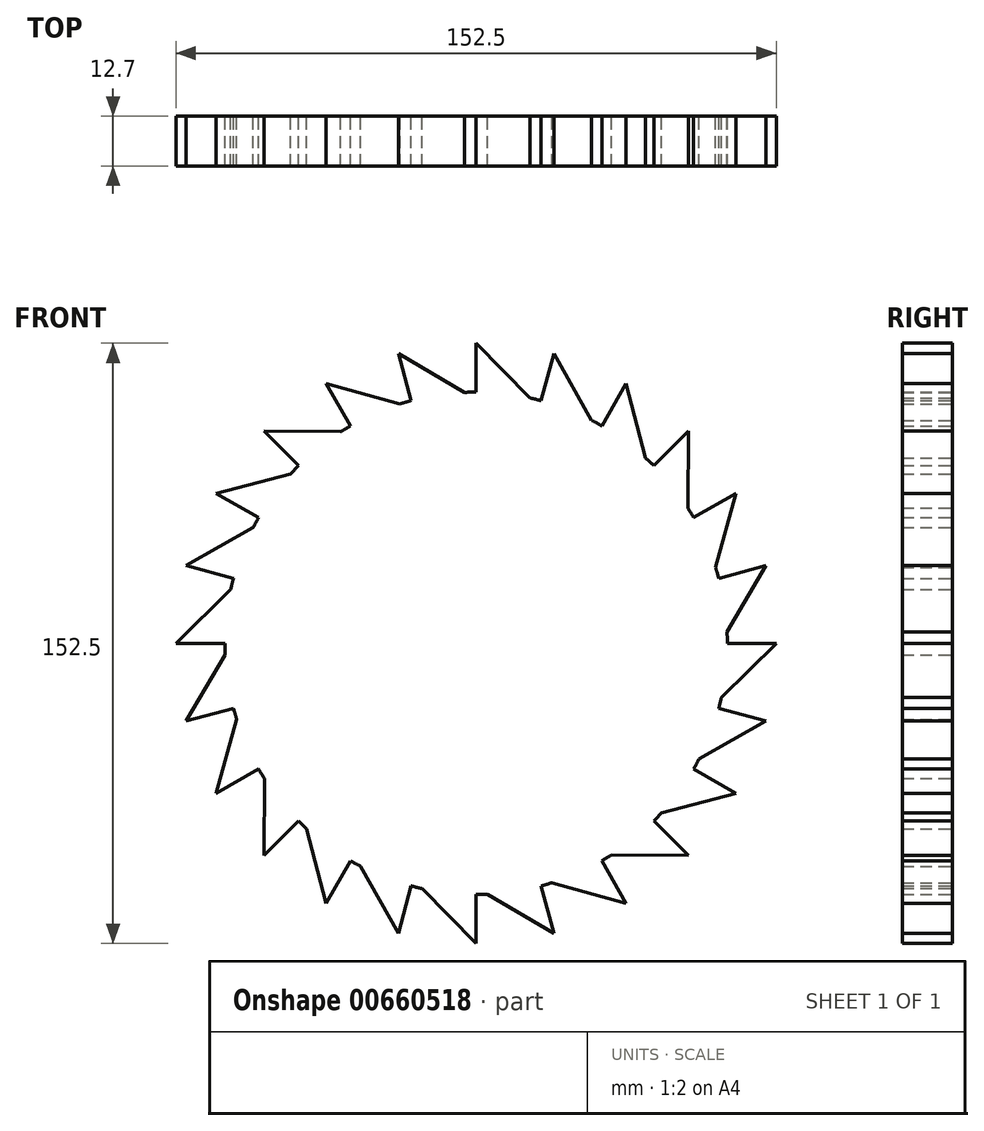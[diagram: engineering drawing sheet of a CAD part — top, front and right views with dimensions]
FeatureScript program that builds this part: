
annotation { "Feature Type Name" : "Feature", "Feature Type Description" : "" }
export const myFeature = defineFeature(function(context is Context, id is Id, definition is map)
    precondition{}
    {
        {
            var Q0;
            Q0=qCreatedBy(makeId("Front.planeOp"),FACE);
            var sketch = newSketch(context, id + "F0", { "sketchPlane" : qUnion([Q0])});
            skCircle(sketch, "E0", {"center": v(0, 0) * mm, "radius": 63.5 * mm, "construction": true});
            skLineSegment(sketch, "E1", {"start": v(0, 63.5) * mm, "end": v(0, 76.25) * mm});
            skLineSegment(sketch, "E2", {"start": v(0, 76.25) * mm, "end": v(14.11, 61.91) * mm});
            skLineSegment(sketch, "E3.1.1", {"start": v(-16.44, 61.34) * mm, "end": v(-19.73, 73.65) * mm});
            skLineSegment(sketch, "E3.1.2", {"start": v(-19.73, 73.65) * mm, "end": v(-2.4, 63.45) * mm});
            skLineSegment(sketch, "E3.2.1", {"start": v(-31.75, 55) * mm, "end": v(-38.13, 66.03) * mm});
            skLineSegment(sketch, "E3.2.2", {"start": v(-38.13, 66.03) * mm, "end": v(-18.74, 60.67) * mm});
            skLineSegment(sketch, "E4.2.3.0", {"start": v(-44.9, 44.9) * mm, "end": v(-53.92, 53.92) * mm});
            skLineSegment(sketch, "E4.5.3.0", {"start": v(-53.92, 53.92) * mm, "end": v(-33.8, 53.76) * mm});
            skLineSegment(sketch, "E4.2.4.0", {"start": v(-55, 31.75) * mm, "end": v(-66.03, 38.13) * mm});
            skLineSegment(sketch, "E4.5.4.0", {"start": v(-66.03, 38.13) * mm, "end": v(-46.56, 43.18) * mm});
            skLineSegment(sketch, "E4.2.5.0", {"start": v(-61.34, 16.44) * mm, "end": v(-73.65, 19.73) * mm});
            skLineSegment(sketch, "E4.5.5.0", {"start": v(-73.65, 19.73) * mm, "end": v(-56.15, 29.65) * mm});
            skLineSegment(sketch, "E4.2.6.0", {"start": v(-63.5, 0) * mm, "end": v(-76.25, 0) * mm});
            skLineSegment(sketch, "E4.5.6.0", {"start": v(-76.25, 0) * mm, "end": v(-61.91, 14.11) * mm});
            skLineSegment(sketch, "E4.2.7.0", {"start": v(-61.34, -16.44) * mm, "end": v(-73.65, -19.73) * mm});
            skLineSegment(sketch, "E4.5.7.0", {"start": v(-73.65, -19.73) * mm, "end": v(-63.45, -2.4) * mm});
            skLineSegment(sketch, "E4.2.8.0", {"start": v(-55, -31.75) * mm, "end": v(-66.03, -38.13) * mm});
            skLineSegment(sketch, "E4.5.8.0", {"start": v(-66.03, -38.13) * mm, "end": v(-60.67, -18.74) * mm});
            skLineSegment(sketch, "E4.2.9.0", {"start": v(-44.9, -44.9) * mm, "end": v(-53.92, -53.92) * mm});
            skLineSegment(sketch, "E4.5.9.0", {"start": v(-53.92, -53.92) * mm, "end": v(-53.76, -33.8) * mm});
            skLineSegment(sketch, "E4.2.10.0", {"start": v(-31.75, -55) * mm, "end": v(-38.13, -66.03) * mm});
            skLineSegment(sketch, "E4.5.10.0", {"start": v(-38.13, -66.03) * mm, "end": v(-43.18, -46.56) * mm});
            skLineSegment(sketch, "E4.2.11.0", {"start": v(-16.44, -61.34) * mm, "end": v(-19.73, -73.65) * mm});
            skLineSegment(sketch, "E4.5.11.0", {"start": v(-19.73, -73.65) * mm, "end": v(-29.65, -56.15) * mm});
            skLineSegment(sketch, "E4.2.12.0", {"start": v(0, -63.5) * mm, "end": v(0, -76.25) * mm});
            skLineSegment(sketch, "E4.5.12.0", {"start": v(0, -76.25) * mm, "end": v(-14.11, -61.91) * mm});
            skLineSegment(sketch, "E4.2.13.0", {"start": v(16.44, -61.34) * mm, "end": v(19.73, -73.65) * mm});
            skLineSegment(sketch, "E4.5.13.0", {"start": v(19.73, -73.65) * mm, "end": v(2.4, -63.45) * mm});
            skLineSegment(sketch, "E4.2.14.0", {"start": v(31.75, -55) * mm, "end": v(38.13, -66.03) * mm});
            skLineSegment(sketch, "E4.5.14.0", {"start": v(38.13, -66.03) * mm, "end": v(18.74, -60.67) * mm});
            skLineSegment(sketch, "E4.2.15.0", {"start": v(44.9, -44.9) * mm, "end": v(53.92, -53.92) * mm});
            skLineSegment(sketch, "E4.5.15.0", {"start": v(53.92, -53.92) * mm, "end": v(33.8, -53.76) * mm});
            skLineSegment(sketch, "E4.2.16.0", {"start": v(55, -31.75) * mm, "end": v(66.03, -38.13) * mm});
            skLineSegment(sketch, "E4.5.16.0", {"start": v(66.03, -38.13) * mm, "end": v(46.56, -43.18) * mm});
            skLineSegment(sketch, "E4.2.17.0", {"start": v(61.34, -16.44) * mm, "end": v(73.65, -19.73) * mm});
            skLineSegment(sketch, "E4.5.17.0", {"start": v(73.65, -19.73) * mm, "end": v(56.15, -29.65) * mm});
            skLineSegment(sketch, "E4.2.18.0", {"start": v(63.5, 0) * mm, "end": v(76.25, 0) * mm});
            skLineSegment(sketch, "E4.5.18.0", {"start": v(76.25, 0) * mm, "end": v(61.91, -14.11) * mm});
            skLineSegment(sketch, "E4.2.19.0", {"start": v(61.34, 16.44) * mm, "end": v(73.65, 19.73) * mm});
            skLineSegment(sketch, "E4.5.19.0", {"start": v(73.65, 19.73) * mm, "end": v(63.45, 2.4) * mm});
            skLineSegment(sketch, "E4.2.20.0", {"start": v(55, 31.75) * mm, "end": v(66.03, 38.13) * mm});
            skLineSegment(sketch, "E4.5.20.0", {"start": v(66.03, 38.13) * mm, "end": v(60.67, 18.74) * mm});
            skLineSegment(sketch, "E4.2.21.0", {"start": v(44.9, 44.9) * mm, "end": v(53.92, 53.92) * mm});
            skLineSegment(sketch, "E4.5.21.0", {"start": v(53.92, 53.92) * mm, "end": v(53.76, 33.8) * mm});
            skLineSegment(sketch, "E4.2.22.0", {"start": v(31.75, 55) * mm, "end": v(38.13, 66.03) * mm});
            skLineSegment(sketch, "E4.5.22.0", {"start": v(38.13, 66.03) * mm, "end": v(43.18, 46.56) * mm});
            skLineSegment(sketch, "E4.2.23.0", {"start": v(16.44, 61.34) * mm, "end": v(19.73, 73.65) * mm});
            skLineSegment(sketch, "E4.5.23.0", {"start": v(19.73, 73.65) * mm, "end": v(29.65, 56.15) * mm});
            skCircle(sketch, "E5", {"center": v(0, 0) * mm, "radius": 63.82 * mm});
            skSolve(sketch);
        }
        {
            var Q0;
            {var subQ0=sQuery(id+"F0.wireOp",EDGE,"E5");var subQ33=makeQuery(id+"F0.imprint","INTERSECT",VERTEX,{"derivedFrom":[sQuery(id+"F0.wireOp",EDGE,"E4.2.18.0"),subQ0]});Q0=makeQuery(id+"F0.imprint","IMPRINT",FACE,{"disambiguationData":[TD([[makeQuery(id+"F0.imprint","IMPRINT",EDGE,{"disambiguationData":[TD([[subQ33,-1.0]])],"derivedFrom":subQ0}),1.0]])]});}
            var Q1;
            {var subQ0=sQuery(id+"F0.wireOp",EDGE,"E4.5.3.0");var subQ1=sQuery(id+"F0.wireOp",EDGE,"E4.2.3.0");var subQ2=makeQuery(id+"F0.imprint","INTERSECT",VERTEX,{"derivedFrom":[subQ1,subQ0]});Q1=makeQuery(id+"F0.imprint","IMPRINT",FACE,{"disambiguationData":[TD([[makeQuery(id+"F0.imprint","IMPRINT",EDGE,{"disambiguationData":[TD([[subQ2,1.0]])],"derivedFrom":subQ1}),-1.0]])]});}
            var Q2;
            {var subQ0=sQuery(id+"F0.wireOp",EDGE,"E3.2.2");var subQ1=sQuery(id+"F0.wireOp",EDGE,"E3.2.1");var subQ2=makeQuery(id+"F0.imprint","INTERSECT",VERTEX,{"derivedFrom":[subQ1,subQ0]});Q2=makeQuery(id+"F0.imprint","IMPRINT",FACE,{"disambiguationData":[TD([[makeQuery(id+"F0.imprint","IMPRINT",EDGE,{"disambiguationData":[TD([[subQ2,1.0]])],"derivedFrom":subQ1}),-1.0]])]});}
            var Q3;
            {var subQ0=sQuery(id+"F0.wireOp",EDGE,"E3.1.2");var subQ1=sQuery(id+"F0.wireOp",EDGE,"E3.1.1");var subQ2=makeQuery(id+"F0.imprint","INTERSECT",VERTEX,{"derivedFrom":[subQ1,subQ0]});Q3=makeQuery(id+"F0.imprint","IMPRINT",FACE,{"disambiguationData":[TD([[makeQuery(id+"F0.imprint","IMPRINT",EDGE,{"disambiguationData":[TD([[subQ2,1.0]])],"derivedFrom":subQ1}),-1.0]])]});}
            var Q4;
            {var subQ0=sQuery(id+"F0.wireOp",EDGE,"E2");var subQ1=sQuery(id+"F0.wireOp",EDGE,"E1");var subQ2=makeQuery(id+"F0.imprint","INTERSECT",VERTEX,{"derivedFrom":[subQ1,subQ0]});Q4=makeQuery(id+"F0.imprint","IMPRINT",FACE,{"disambiguationData":[TD([[makeQuery(id+"F0.imprint","IMPRINT",EDGE,{"disambiguationData":[TD([[subQ2,1.0]])],"derivedFrom":subQ1}),-1.0]])]});}
            var Q5;
            {var subQ0=sQuery(id+"F0.wireOp",EDGE,"E4.5.23.0");var subQ1=sQuery(id+"F0.wireOp",EDGE,"E4.2.23.0");var subQ2=makeQuery(id+"F0.imprint","INTERSECT",VERTEX,{"derivedFrom":[subQ1,subQ0]});Q5=makeQuery(id+"F0.imprint","IMPRINT",FACE,{"disambiguationData":[TD([[makeQuery(id+"F0.imprint","IMPRINT",EDGE,{"disambiguationData":[TD([[subQ2,1.0]])],"derivedFrom":subQ1}),-1.0]])]});}
            var Q6;
            {var subQ0=sQuery(id+"F0.wireOp",EDGE,"E4.5.22.0");var subQ1=sQuery(id+"F0.wireOp",EDGE,"E4.2.22.0");var subQ2=makeQuery(id+"F0.imprint","INTERSECT",VERTEX,{"derivedFrom":[subQ1,subQ0]});Q6=makeQuery(id+"F0.imprint","IMPRINT",FACE,{"disambiguationData":[TD([[makeQuery(id+"F0.imprint","IMPRINT",EDGE,{"disambiguationData":[TD([[subQ2,1.0]])],"derivedFrom":subQ1}),-1.0]])]});}
            var Q7;
            {var subQ0=sQuery(id+"F0.wireOp",EDGE,"E4.5.21.0");var subQ1=sQuery(id+"F0.wireOp",EDGE,"E4.2.21.0");var subQ2=makeQuery(id+"F0.imprint","INTERSECT",VERTEX,{"derivedFrom":[subQ1,subQ0]});Q7=makeQuery(id+"F0.imprint","IMPRINT",FACE,{"disambiguationData":[TD([[makeQuery(id+"F0.imprint","IMPRINT",EDGE,{"disambiguationData":[TD([[subQ2,1.0]])],"derivedFrom":subQ1}),-1.0]])]});}
            var Q8;
            {var subQ0=sQuery(id+"F0.wireOp",EDGE,"E4.5.20.0");var subQ1=sQuery(id+"F0.wireOp",EDGE,"E4.2.20.0");var subQ2=makeQuery(id+"F0.imprint","INTERSECT",VERTEX,{"derivedFrom":[subQ1,subQ0]});Q8=makeQuery(id+"F0.imprint","IMPRINT",FACE,{"disambiguationData":[TD([[makeQuery(id+"F0.imprint","IMPRINT",EDGE,{"disambiguationData":[TD([[subQ2,1.0]])],"derivedFrom":subQ1}),-1.0]])]});}
            var Q9;
            {var subQ0=sQuery(id+"F0.wireOp",EDGE,"E4.5.19.0");var subQ1=sQuery(id+"F0.wireOp",EDGE,"E4.2.19.0");var subQ2=makeQuery(id+"F0.imprint","INTERSECT",VERTEX,{"derivedFrom":[subQ1,subQ0]});Q9=makeQuery(id+"F0.imprint","IMPRINT",FACE,{"disambiguationData":[TD([[makeQuery(id+"F0.imprint","IMPRINT",EDGE,{"disambiguationData":[TD([[subQ2,1.0]])],"derivedFrom":subQ1}),-1.0]])]});}
            var Q10;
            {var subQ0=sQuery(id+"F0.wireOp",EDGE,"E4.5.18.0");var subQ1=sQuery(id+"F0.wireOp",EDGE,"E4.2.18.0");var subQ2=makeQuery(id+"F0.imprint","INTERSECT",VERTEX,{"derivedFrom":[subQ1,subQ0]});Q10=makeQuery(id+"F0.imprint","IMPRINT",FACE,{"disambiguationData":[TD([[makeQuery(id+"F0.imprint","IMPRINT",EDGE,{"disambiguationData":[TD([[subQ2,1.0]])],"derivedFrom":subQ1}),-1.0]])]});}
            var Q11;
            {var subQ0=sQuery(id+"F0.wireOp",EDGE,"E4.5.17.0");var subQ1=sQuery(id+"F0.wireOp",EDGE,"E4.2.17.0");var subQ2=makeQuery(id+"F0.imprint","INTERSECT",VERTEX,{"derivedFrom":[subQ1,subQ0]});Q11=makeQuery(id+"F0.imprint","IMPRINT",FACE,{"disambiguationData":[TD([[makeQuery(id+"F0.imprint","IMPRINT",EDGE,{"disambiguationData":[TD([[subQ2,1.0]])],"derivedFrom":subQ1}),-1.0]])]});}
            var Q12;
            {var subQ0=sQuery(id+"F0.wireOp",EDGE,"E4.5.16.0");var subQ1=sQuery(id+"F0.wireOp",EDGE,"E4.2.16.0");var subQ2=makeQuery(id+"F0.imprint","INTERSECT",VERTEX,{"derivedFrom":[subQ1,subQ0]});Q12=makeQuery(id+"F0.imprint","IMPRINT",FACE,{"disambiguationData":[TD([[makeQuery(id+"F0.imprint","IMPRINT",EDGE,{"disambiguationData":[TD([[subQ2,1.0]])],"derivedFrom":subQ1}),-1.0]])]});}
            var Q13;
            {var subQ0=sQuery(id+"F0.wireOp",EDGE,"E4.5.15.0");var subQ1=sQuery(id+"F0.wireOp",EDGE,"E4.2.15.0");var subQ2=makeQuery(id+"F0.imprint","INTERSECT",VERTEX,{"derivedFrom":[subQ1,subQ0]});Q13=makeQuery(id+"F0.imprint","IMPRINT",FACE,{"disambiguationData":[TD([[makeQuery(id+"F0.imprint","IMPRINT",EDGE,{"disambiguationData":[TD([[subQ2,1.0]])],"derivedFrom":subQ1}),-1.0]])]});}
            var Q14;
            {var subQ0=sQuery(id+"F0.wireOp",EDGE,"E4.5.14.0");var subQ1=sQuery(id+"F0.wireOp",EDGE,"E4.2.14.0");var subQ2=makeQuery(id+"F0.imprint","INTERSECT",VERTEX,{"derivedFrom":[subQ1,subQ0]});Q14=makeQuery(id+"F0.imprint","IMPRINT",FACE,{"disambiguationData":[TD([[makeQuery(id+"F0.imprint","IMPRINT",EDGE,{"disambiguationData":[TD([[subQ2,1.0]])],"derivedFrom":subQ1}),-1.0]])]});}
            var Q15;
            {var subQ0=sQuery(id+"F0.wireOp",EDGE,"E4.5.13.0");var subQ1=sQuery(id+"F0.wireOp",EDGE,"E4.2.13.0");var subQ2=makeQuery(id+"F0.imprint","INTERSECT",VERTEX,{"derivedFrom":[subQ1,subQ0]});Q15=makeQuery(id+"F0.imprint","IMPRINT",FACE,{"disambiguationData":[TD([[makeQuery(id+"F0.imprint","IMPRINT",EDGE,{"disambiguationData":[TD([[subQ2,1.0]])],"derivedFrom":subQ1}),-1.0]])]});}
            var Q16;
            {var subQ0=sQuery(id+"F0.wireOp",EDGE,"E4.5.12.0");var subQ1=sQuery(id+"F0.wireOp",EDGE,"E4.2.12.0");var subQ2=makeQuery(id+"F0.imprint","INTERSECT",VERTEX,{"derivedFrom":[subQ1,subQ0]});Q16=makeQuery(id+"F0.imprint","IMPRINT",FACE,{"disambiguationData":[TD([[makeQuery(id+"F0.imprint","IMPRINT",EDGE,{"disambiguationData":[TD([[subQ2,1.0]])],"derivedFrom":subQ1}),-1.0]])]});}
            var Q17;
            {var subQ0=sQuery(id+"F0.wireOp",EDGE,"E4.5.11.0");var subQ1=sQuery(id+"F0.wireOp",EDGE,"E4.2.11.0");var subQ2=makeQuery(id+"F0.imprint","INTERSECT",VERTEX,{"derivedFrom":[subQ1,subQ0]});Q17=makeQuery(id+"F0.imprint","IMPRINT",FACE,{"disambiguationData":[TD([[makeQuery(id+"F0.imprint","IMPRINT",EDGE,{"disambiguationData":[TD([[subQ2,1.0]])],"derivedFrom":subQ1}),-1.0]])]});}
            var Q18;
            {var subQ0=sQuery(id+"F0.wireOp",EDGE,"E4.5.10.0");var subQ1=sQuery(id+"F0.wireOp",EDGE,"E4.2.10.0");var subQ2=makeQuery(id+"F0.imprint","INTERSECT",VERTEX,{"derivedFrom":[subQ1,subQ0]});Q18=makeQuery(id+"F0.imprint","IMPRINT",FACE,{"disambiguationData":[TD([[makeQuery(id+"F0.imprint","IMPRINT",EDGE,{"disambiguationData":[TD([[subQ2,1.0]])],"derivedFrom":subQ1}),-1.0]])]});}
            var Q19;
            {var subQ0=sQuery(id+"F0.wireOp",EDGE,"E4.5.8.0");var subQ1=sQuery(id+"F0.wireOp",EDGE,"E4.2.8.0");var subQ2=makeQuery(id+"F0.imprint","INTERSECT",VERTEX,{"derivedFrom":[subQ1,subQ0]});Q19=makeQuery(id+"F0.imprint","IMPRINT",FACE,{"disambiguationData":[TD([[makeQuery(id+"F0.imprint","IMPRINT",EDGE,{"disambiguationData":[TD([[subQ2,1.0]])],"derivedFrom":subQ1}),-1.0]])]});}
            var Q20;
            {var subQ0=sQuery(id+"F0.wireOp",EDGE,"E4.5.7.0");var subQ1=sQuery(id+"F0.wireOp",EDGE,"E4.2.7.0");var subQ2=makeQuery(id+"F0.imprint","INTERSECT",VERTEX,{"derivedFrom":[subQ1,subQ0]});Q20=makeQuery(id+"F0.imprint","IMPRINT",FACE,{"disambiguationData":[TD([[makeQuery(id+"F0.imprint","IMPRINT",EDGE,{"disambiguationData":[TD([[subQ2,1.0]])],"derivedFrom":subQ1}),-1.0]])]});}
            var Q21;
            {var subQ0=sQuery(id+"F0.wireOp",EDGE,"E4.5.6.0");var subQ1=sQuery(id+"F0.wireOp",EDGE,"E4.2.6.0");var subQ2=makeQuery(id+"F0.imprint","INTERSECT",VERTEX,{"derivedFrom":[subQ1,subQ0]});Q21=makeQuery(id+"F0.imprint","IMPRINT",FACE,{"disambiguationData":[TD([[makeQuery(id+"F0.imprint","IMPRINT",EDGE,{"disambiguationData":[TD([[subQ2,1.0]])],"derivedFrom":subQ1}),-1.0]])]});}
            var Q22;
            {var subQ0=sQuery(id+"F0.wireOp",EDGE,"E4.5.5.0");var subQ1=sQuery(id+"F0.wireOp",EDGE,"E4.2.5.0");var subQ2=makeQuery(id+"F0.imprint","INTERSECT",VERTEX,{"derivedFrom":[subQ1,subQ0]});Q22=makeQuery(id+"F0.imprint","IMPRINT",FACE,{"disambiguationData":[TD([[makeQuery(id+"F0.imprint","IMPRINT",EDGE,{"disambiguationData":[TD([[subQ2,1.0]])],"derivedFrom":subQ1}),-1.0]])]});}
            var Q23;
            {var subQ0=sQuery(id+"F0.wireOp",EDGE,"E4.5.4.0");var subQ1=sQuery(id+"F0.wireOp",EDGE,"E4.2.4.0");var subQ2=makeQuery(id+"F0.imprint","INTERSECT",VERTEX,{"derivedFrom":[subQ1,subQ0]});Q23=makeQuery(id+"F0.imprint","IMPRINT",FACE,{"disambiguationData":[TD([[makeQuery(id+"F0.imprint","IMPRINT",EDGE,{"disambiguationData":[TD([[subQ2,1.0]])],"derivedFrom":subQ1}),-1.0]])]});}
            var Q24;
            {var subQ0=sQuery(id+"F0.wireOp",EDGE,"E4.5.9.0");var subQ1=sQuery(id+"F0.wireOp",EDGE,"E4.2.9.0");var subQ2=makeQuery(id+"F0.imprint","INTERSECT",VERTEX,{"derivedFrom":[subQ1,subQ0]});Q24=makeQuery(id+"F0.imprint","IMPRINT",FACE,{"disambiguationData":[TD([[makeQuery(id+"F0.imprint","IMPRINT",EDGE,{"disambiguationData":[TD([[subQ2,1.0]])],"derivedFrom":subQ1}),-1.0]])]});}
            extrude(context, id + "F1", {"entities" : qUnion([Q0, Q1, Q2, Q3, Q4, Q5, Q6, Q7, Q8, Q9, Q10, Q11, Q12, Q13, Q14, Q15, Q16, Q17, Q18, Q19, Q20, Q21, Q22, Q23, Q24]), "depth" : 12.7 * mm, "offsetDistance" : 25.4 * mm});
        }
    });
